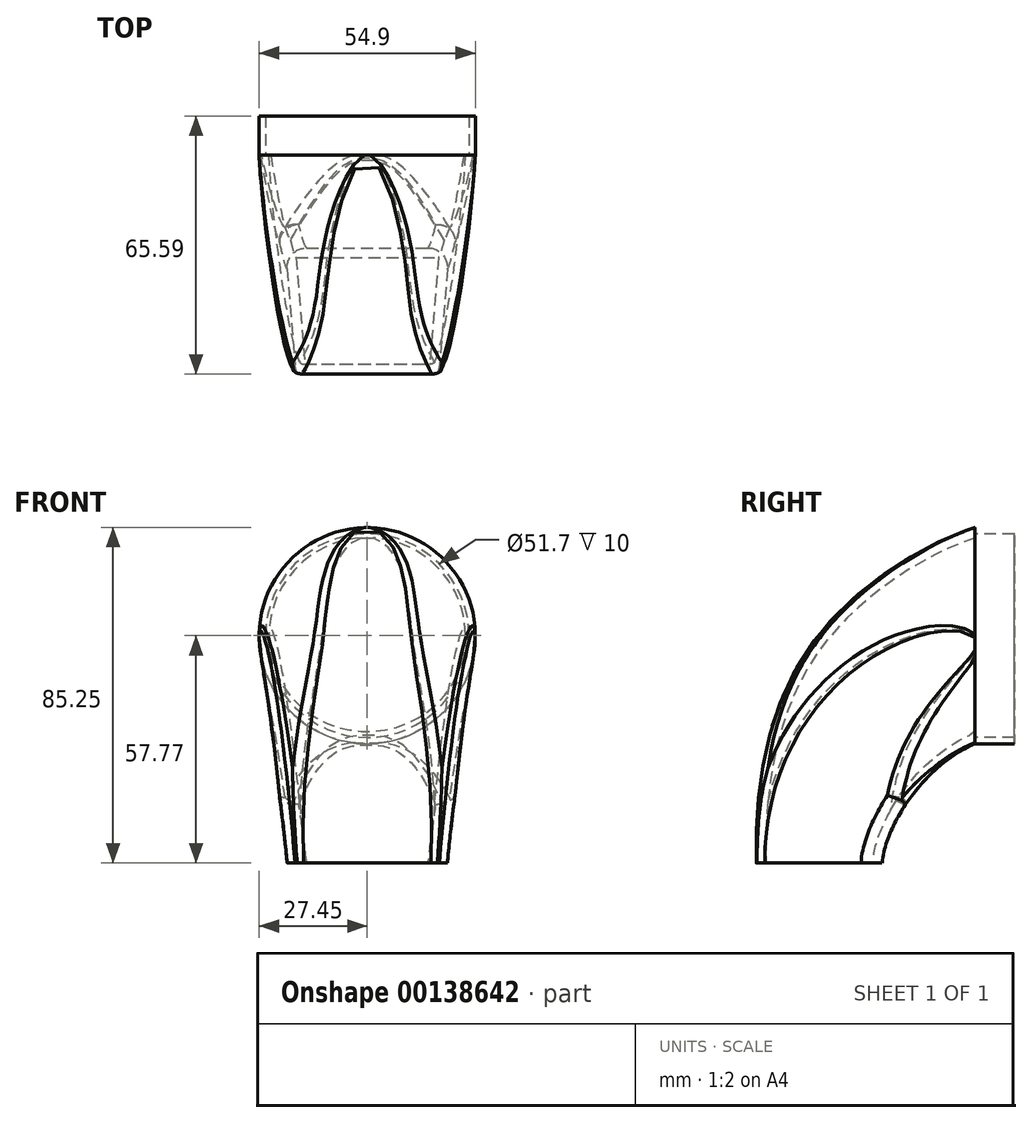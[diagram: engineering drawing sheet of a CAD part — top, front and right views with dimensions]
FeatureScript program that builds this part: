
annotation { "Feature Type Name" : "Feature", "Feature Type Description" : "" }
export const myFeature = defineFeature(function(context is Context, id is Id, definition is map)
    precondition{}
    {
        {
            var Q0;
            Q0=qCreatedBy(makeId("Front.planeOp"),FACE);
            var sketch = newSketch(context, id + "F0", { "sketchPlane" : qUnion([Q0])});
            skCircle(sketch, "E0", {"center": v(0, 0) * mm, "radius": 25.85 * mm});
            skLineSegment(sketch, "E1", {"start": v(-10.5, 25.36) * mm, "end": v(-10.5, 25.36) * mm});
            skCircle(sketch, "E2.0", {"center": v(0, 0) * mm, "radius": 27.45 * mm});
            skSolve(sketch);
        }
        {
            var Q0;
            Q0=makeQuery(id+"F0.imprint","IMPRINT",FACE,{"disambiguationData":[TD([[makeQuery(id+"F0.imprint","IMPRINT",EDGE,{"derivedFrom":sQuery(id+"F0.wireOp",EDGE,"E2.0")}),1.0]])]});
            cPlane(context, id + "F1", {"entities" : qUnion([Q0]), "cplaneType" : CPlaneType.OFFSET, "offset" : 20 * mm, "oppositeDirection" : true, "width" : 150 * mm, "height" : 150 * mm});
        }
        {
            var Q0;
            Q0=qCreatedBy(id+"F1.planeOp",FACE);
            var sketch = newSketch(context, id + "F2", { "sketchPlane" : qUnion([Q0])});
            skLineSegment(sketch, "E3", {"start": v(-43.93, -52.45) * mm, "end": v(39.9, -52.45) * mm, "construction": true});
            skSolve(sketch);
        }
        {
            var Q0;
            Q0=makeQuery(id+"F0.imprint","IMPRINT",FACE,{"disambiguationData":[TD([[makeQuery(id+"F0.imprint","IMPRINT",EDGE,{"derivedFrom":sQuery(id+"F0.wireOp",EDGE,"E2.0")}),1.0]])]});
            var Q1;
            Q1=makeQuery(id+"F0.imprint","IMPRINT",FACE,{"disambiguationData":[TD([[makeQuery(id+"F0.imprint","IMPRINT",EDGE,{"derivedFrom":sQuery(id+"F0.wireOp",EDGE,"E0")}),1.0]])]});
            var Q2;
            Q2=sQuery(id+"F2.wireOp",EDGE,"E3");
            revolve(context, id + "F3", {"entities" : qUnion([Q0, Q1]), "axis" : qUnion([Q2]), "revolveType" : RevolveType.ONE_DIRECTION, "angle" : 80 * degree});
        }
        {
            var Q0;
            Q0=qCreatedBy(makeId("Right.planeOp"),FACE);
            var sketch = newSketch(context, id + "F4", { "sketchPlane" : qUnion([Q0])});
            skFitSpline(sketch, "E4", {"points": [v(0, 27.45) * mm, v(-39.78, 0) * mm, v(-55.53, -57.77) * mm], "startDerivative": vector(-73.1, -22.38) * mm, "endDerivative": vector(3.27, -125.86) * mm});
            skFitSpline(sketch, "E5", {"points": [v(0, -27.45) * mm, v(-15.95, -40.58) * mm, v(-23.53, -57.77) * mm], "startDerivative": vector(-27.77, -10.54) * mm, "endDerivative": vector(-1.32, -26.27) * mm});
            skLineSegment(sketch, "E6", {"start": v(0, -27.45) * mm, "end": v(0, -69.1) * mm});
            skLineSegment(sketch, "E7", {"start": v(0, -69.1) * mm, "end": v(-79.68, -69.1) * mm});
            skLineSegment(sketch, "E8", {"start": v(-79.68, -69.1) * mm, "end": v(-79.68, 27.45) * mm});
            skLineSegment(sketch, "E9", {"start": v(-79.68, 27.45) * mm, "end": v(0, 27.45) * mm});
            skLineSegment(sketch, "E10", {"start": v(-23.53, -57.77) * mm, "end": v(-55.53, -57.77) * mm});
            skSolve(sketch);
        }
        {
            var Q0;
            Q0=makeQuery(id+"F4.imprint","IMPRINT",FACE,{"disambiguationData":[TD([[makeQuery(id+"F4.imprint","IMPRINT",EDGE,{"derivedFrom":sQuery(id+"F4.wireOp",EDGE,"E4")}),-1.0]])]});
            var Q1;
            Q1=makeQuery(id+"F3.opRevolve","SWEPT_BODY",BODY,{"disambiguationData":[OSD([sQuery(id+"F0.wireOp",EDGE,"E2.0")])]});
            var Q2;
            Q2=makeQuery(id+"F3.opRevolve","SWEPT_BODY",BODY,{"disambiguationData":[OSD([sQuery(id+"F0.wireOp",EDGE,"E2.0")])]});
            extrude(context, id + "F5", {"entities" : qUnion([Q0]), "operationType" : NewBodyOperationType.REMOVE, "endBound" : BoundingType.THROUGH_ALL, "oppositeDirection" : true, "endBoundEntityBody" : qUnion([Q1]), "depth" : 25 * mm, "hasSecondDirection" : true, "secondDirectionBound" : SecondDirectionBoundingType.THROUGH_ALL, "secondDirectionOppositeDirection" : false, "secondDirectionBoundEntityBody" : qUnion([Q2]), "secondDirectionDepth" : 25 * mm});
        }
        {
            var Q0;
            Q0=qCreatedBy(makeId("Top.planeOp"),FACE);
            var Q1;
            Q1=qCreatedBy(makeId("Front.planeOp"),FACE);
            cPlane(context, id + "F6", {"entities" : qUnion([Q0, Q1]), "cplaneType" : CPlaneType.MID_PLANE, "offset" : 25 * mm, "flipAlignment" : true, "width" : 150 * mm, "height" : 150 * mm});
        }
        {
            var Q0;
            Q0=qCreatedBy(id+"F6.planeOp",FACE);
            var sketch = newSketch(context, id + "F7", { "sketchPlane" : qUnion([Q0])});
            skLineSegment(sketch, "E11", {"start": v(27.45, 0) * mm, "end": v(18.16, -80.12) * mm});
            skLineSegment(sketch, "E12", {"start": v(18.16, -80.12) * mm, "end": v(35.32, -80.12) * mm});
            skLineSegment(sketch, "E13", {"start": v(35.32, -80.12) * mm, "end": v(35.32, 0) * mm});
            skLineSegment(sketch, "E14", {"start": v(35.32, 0) * mm, "end": v(27.45, 0) * mm});
            skLineSegment(sketch, "E15", {"start": v(-27.45, 0) * mm, "end": v(-18.16, -80.12) * mm});
            skLineSegment(sketch, "E16", {"start": v(-18.16, -80.12) * mm, "end": v(-35.18, -80.12) * mm});
            skLineSegment(sketch, "E17", {"start": v(-35.18, -80.12) * mm, "end": v(-35.18, 0) * mm});
            skLineSegment(sketch, "E18", {"start": v(-35.18, 0) * mm, "end": v(-27.45, 0) * mm});
            skSolve(sketch);
        }
        {
            var Q0;
            Q0=makeQuery(id+"F7.imprint","IMPRINT",FACE,{"disambiguationData":[TD([[makeQuery(id+"F7.imprint","IMPRINT",EDGE,{"derivedFrom":sQuery(id+"F7.wireOp",EDGE,"E15")}),-1.0]])]});
            var Q1;
            Q1=makeQuery(id+"F7.imprint","IMPRINT",FACE,{"disambiguationData":[TD([[makeQuery(id+"F7.imprint","IMPRINT",EDGE,{"derivedFrom":sQuery(id+"F7.wireOp",EDGE,"E11")}),1.0]])]});
            extrude(context, id + "F8", {"entities" : qUnion([Q0, Q1]), "operationType" : NewBodyOperationType.REMOVE, "endBound" : BoundingType.THROUGH_ALL, "oppositeDirection" : true, "depth" : 25 * mm, "hasSecondDirection" : true, "secondDirectionBound" : SecondDirectionBoundingType.THROUGH_ALL, "secondDirectionOppositeDirection" : false, "secondDirectionDepth" : 25 * mm});
        }
        {
            var Q0;
            Q0=makeQuery(id+"F5.boolean.opBoolean","COPY",FACE,{"derivedFrom":makeQuery(id+"F5.opExtrude","SWEPT_FACE",FACE,{"disambiguationData":[OSD([sQuery(id+"F4.wireOp",EDGE,"E10")])]})});
            var Q1;
            Q1=makeQuery(id+"F3.opRevolve","CAP_FACE",FACE,{"disambiguationData":[OSD([sQuery(id+"F0.wireOp",EDGE,"E2.0")])],"isStart":true});
            shell(context, id + "F9", {"entities" : qUnion([Q0, Q1]), "thickness" : 2.5 * mm});
        }
        {
            var Q0;
            Q0=makeQuery(id+"F5.boolean.opBoolean","INTERSECT",EDGE,{"disambiguationData":[OD(1.0)],"derivedFrom":[makeQuery(id+"F3.opRevolve","SWEPT_FACE",FACE,{"disambiguationData":[OSD([sQuery(id+"F0.wireOp",EDGE,"E2.0")])]}),makeQuery(id+"F5.opExtrude","SWEPT_FACE",FACE,{"disambiguationData":[OSD([sQuery(id+"F4.wireOp",EDGE,"E4")])]})]});
            var Q1;
            Q1=makeQuery(id+"F8.boolean.opBoolean","INTERSECT",EDGE,{"disambiguationData":[OD(0.0)],"derivedFrom":[makeQuery(id+"F5.boolean.opBoolean","SPLIT",FACE,{"disambiguationData":[OD(1.0)],"derivedFrom":makeQuery(id+"F3.opRevolve","SWEPT_FACE",FACE,{"disambiguationData":[OSD([sQuery(id+"F0.wireOp",EDGE,"E2.0")])]})}),makeQuery(id+"F8.opExtrude","SWEPT_FACE",FACE,{"disambiguationData":[OSD([sQuery(id+"F7.wireOp",EDGE,"E11")])]})]});
            var Q2;
            Q2=makeQuery(id+"F8.boolean.opBoolean","INTERSECT",EDGE,{"disambiguationData":[OD(0.0)],"derivedFrom":[makeQuery(id+"F5.boolean.opBoolean","SPLIT",FACE,{"disambiguationData":[OD(0.0)],"derivedFrom":makeQuery(id+"F3.opRevolve","SWEPT_FACE",FACE,{"disambiguationData":[OSD([sQuery(id+"F0.wireOp",EDGE,"E2.0")])]})}),makeQuery(id+"F8.opExtrude","SWEPT_FACE",FACE,{"disambiguationData":[OSD([sQuery(id+"F7.wireOp",EDGE,"E15")])]})]});
            var Q3;
            Q3=makeQuery(id+"F8.boolean.opBoolean","INTERSECT",EDGE,{"disambiguationData":[OD(1.0)],"derivedFrom":[makeQuery(id+"F5.boolean.opBoolean","SPLIT",FACE,{"disambiguationData":[OD(0.0)],"derivedFrom":makeQuery(id+"F3.opRevolve","SWEPT_FACE",FACE,{"disambiguationData":[OSD([sQuery(id+"F0.wireOp",EDGE,"E2.0")])]})}),makeQuery(id+"F8.opExtrude","SWEPT_FACE",FACE,{"disambiguationData":[OSD([sQuery(id+"F7.wireOp",EDGE,"E15")])]})]});
            var Q4;
            Q4=makeQuery(id+"F5.boolean.opBoolean","INTERSECT",EDGE,{"disambiguationData":[OD(0.0)],"derivedFrom":[makeQuery(id+"F3.opRevolve","SWEPT_FACE",FACE,{"disambiguationData":[OSD([sQuery(id+"F0.wireOp",EDGE,"E2.0")])]}),makeQuery(id+"F5.opExtrude","SWEPT_FACE",FACE,{"disambiguationData":[OSD([sQuery(id+"F4.wireOp",EDGE,"E5")])]})]});
            var Q5;
            Q5=makeQuery(id+"F8.boolean.opBoolean","INTERSECT",EDGE,{"disambiguationData":[OD(1.0)],"derivedFrom":[makeQuery(id+"F5.boolean.opBoolean","SPLIT",FACE,{"disambiguationData":[OD(1.0)],"derivedFrom":makeQuery(id+"F3.opRevolve","SWEPT_FACE",FACE,{"disambiguationData":[OSD([sQuery(id+"F0.wireOp",EDGE,"E2.0")])]})}),makeQuery(id+"F8.opExtrude","SWEPT_FACE",FACE,{"disambiguationData":[OSD([sQuery(id+"F7.wireOp",EDGE,"E11")])]})]});
            var Q6;
            Q6=makeQuery(id+"F8.boolean.opBoolean","INTERSECT",EDGE,{"derivedFrom":[makeQuery(id+"F5.boolean.opBoolean","COPY",FACE,{"derivedFrom":makeQuery(id+"F5.opExtrude","SWEPT_FACE",FACE,{"disambiguationData":[OSD([sQuery(id+"F4.wireOp",EDGE,"E5")])]})}),makeQuery(id+"F8.opExtrude","SWEPT_FACE",FACE,{"disambiguationData":[OSD([sQuery(id+"F7.wireOp",EDGE,"E11")])]})]});
            var Q7;
            Q7=makeQuery(id+"F8.boolean.opBoolean","INTERSECT",EDGE,{"derivedFrom":[makeQuery(id+"F5.boolean.opBoolean","COPY",FACE,{"derivedFrom":makeQuery(id+"F5.opExtrude","SWEPT_FACE",FACE,{"disambiguationData":[OSD([sQuery(id+"F4.wireOp",EDGE,"E5")])]})}),makeQuery(id+"F8.opExtrude","SWEPT_FACE",FACE,{"disambiguationData":[OSD([sQuery(id+"F7.wireOp",EDGE,"E15")])]})]});
            fillet(context, id + "F10", {"entities" : qUnion([Q0, Q1, Q2, Q3, Q4, Q5, Q6, Q7]), "radius" : 5 * mm, "tangentPropagation" : true, "allowEdgeOverflow" : false});
        }
        {
            var Q0;
            Q0=makeQuery(id+"F0.imprint","IMPRINT",FACE,{"disambiguationData":[TD([[makeQuery(id+"F0.imprint","IMPRINT",EDGE,{"derivedFrom":sQuery(id+"F0.wireOp",EDGE,"E2.0")}),1.0]])]});
            extrude(context, id + "F11", {"entities" : qUnion([Q0]), "operationType" : NewBodyOperationType.ADD, "oppositeDirection" : true, "depth" : 10 * mm});
        }
    });
